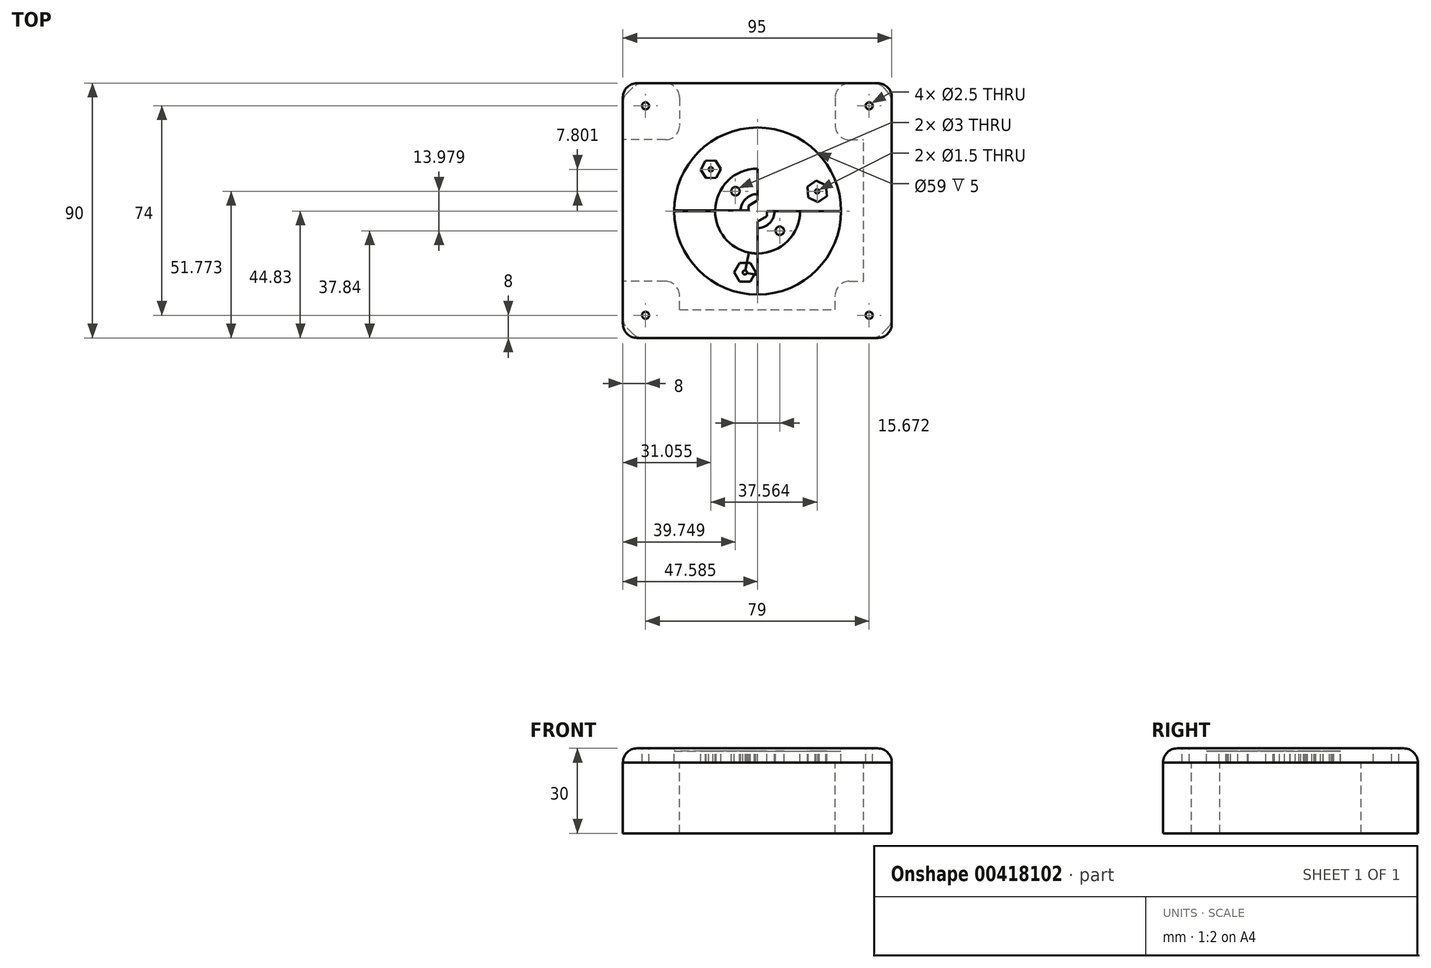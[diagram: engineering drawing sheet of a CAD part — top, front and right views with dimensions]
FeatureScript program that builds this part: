
annotation { "Feature Type Name" : "Feature", "Feature Type Description" : "" }
export const myFeature = defineFeature(function(context is Context, id is Id, definition is map)
    precondition{}
    {
        {
            var Q0;
            Q0=qCreatedBy(makeId("Top.planeOp"),FACE);
            var sketch = newSketch(context, id + "F0", { "sketchPlane" : qUnion([Q0])});
            skLineSegment(sketch, "E0", {"start": v(0, 0) * mm, "end": v(-47.5, 0) * mm});
            skLineSegment(sketch, "E1", {"start": v(-47.5, 0) * mm, "end": v(-47.5, 45) * mm});
            skLineSegment(sketch, "E2", {"start": v(-47.5, 45) * mm, "end": v(0, 45) * mm});
            skLineSegment(sketch, "E3.MirrorCS", {"start": v(47.5, 45) * mm, "end": v(0, 45) * mm});
            skLineSegment(sketch, "E4.MirrorCS", {"start": v(47.5, 0) * mm, "end": v(47.5, 45) * mm});
            skLineSegment(sketch, "E5.MirrorCS", {"start": v(-47.5, 0) * mm, "end": v(-47.5, -45) * mm});
            skLineSegment(sketch, "E6.MirrorCS", {"start": v(-47.5, -45) * mm, "end": v(0, -45) * mm});
            skLineSegment(sketch, "E7.MirrorCS", {"start": v(47.5, -45) * mm, "end": v(0, -45) * mm});
            skLineSegment(sketch, "E8.MirrorCS", {"start": v(47.5, 0) * mm, "end": v(47.5, -45) * mm});
            skLineSegment(sketch, "E9", {"start": v(-47.5, 45) * mm, "end": v(-39.5, 45) * mm});
            skLineSegment(sketch, "E10", {"start": v(-39.5, 45) * mm, "end": v(-39.5, 37) * mm});
            skCircle(sketch, "E11", {"center": v(-39.5, 37) * mm, "radius": 1.25 * mm});
            skCircle(sketch, "E12.MirrorC", {"center": v(-39.5, -37) * mm, "radius": 1.25 * mm});
            skLineSegment(sketch, "E13", {"start": v(0, 45) * mm, "end": v(0, 44.66) * mm});
            skCircle(sketch, "E14.MirrorC", {"center": v(39.5, 37) * mm, "radius": 1.25 * mm});
            skCircle(sketch, "E15.MirrorC", {"center": v(39.5, -37) * mm, "radius": 1.25 * mm});
            skCircle(sketch, "E16", {"center": v(0.08, -0.17) * mm, "radius": 29.5 * mm});
            skLineSegment(sketch, "E17", {"start": v(0.08, -0.17) * mm, "end": v(0.08, 29.33) * mm});
            skLineSegment(sketch, "E18", {"start": v(0.08, 29.33) * mm, "end": v(0.08, -29.67) * mm});
            skLineSegment(sketch, "E19", {"start": v(-29.42, -0.17) * mm, "end": v(29.58, -0.17) * mm});
            skLineSegment(sketch, "E20", {"start": v(0.08, -0.17) * mm, "end": v(-4.42, -21.86) * mm});
            skLineSegment(sketch, "E21", {"start": v(-4.42, -21.86) * mm, "end": v(0.08, -22.8) * mm});
            skCircle(sketch, "E22", {"center": v(-4.42, -21.86) * mm, "radius": 0.75 * mm});
            skCircle(sketch, "E23", {"center": v(21.12, 6.77) * mm, "radius": 0.75 * mm});
            skCircle(sketch, "E24", {"center": v(-16.44, 14.57) * mm, "radius": 0.75 * mm});
            skCircle(sketch, "E25.cCircle", {"center": v(0.08, -0.17) * mm, "radius": 3.25 * mm, "construction": true});
            skLineSegment(sketch, "E25.0", {"start": v(3.33, 1.7) * mm, "end": v(3.33, -2.05) * mm});
            skLineSegment(sketch, "E25.1", {"start": v(3.33, -2.05) * mm, "end": v(0.08, -3.92) * mm});
            skLineSegment(sketch, "E25.2", {"start": v(0.08, -3.92) * mm, "end": v(-3.17, -2.05) * mm});
            skLineSegment(sketch, "E25.3", {"start": v(-3.17, -2.05) * mm, "end": v(-3.17, 1.7) * mm});
            skLineSegment(sketch, "E25.4", {"start": v(-3.17, 1.7) * mm, "end": v(0.08, 3.58) * mm});
            skLineSegment(sketch, "E25.5", {"start": v(0.08, 3.58) * mm, "end": v(3.33, 1.7) * mm});
            skPoint(sketch, "E25.0.midPoint", {"position": v(3.33, -0.17) * mm});
            skCircle(sketch, "E26", {"center": v(0.08, -0.17) * mm, "radius": 6 * mm});
            skCircle(sketch, "E27", {"center": v(0.08, -0.17) * mm, "radius": 15 * mm});
            skLineSegment(sketch, "E28", {"start": v(8.87, -28.33) * mm, "end": v(8.87, -25.44) * mm});
            skCircle(sketch, "E29.cCircle", {"center": v(-16.44, 14.57) * mm, "radius": 3.06 * mm, "construction": true});
            skLineSegment(sketch, "E29.0", {"start": v(-14.8, 17.7) * mm, "end": v(-12.91, 14.7) * mm});
            skLineSegment(sketch, "E29.1", {"start": v(-12.91, 14.7) * mm, "end": v(-14.56, 11.58) * mm});
            skLineSegment(sketch, "E29.2", {"start": v(-14.56, 11.58) * mm, "end": v(-18.1, 11.45) * mm});
            skLineSegment(sketch, "E29.3", {"start": v(-18.1, 11.45) * mm, "end": v(-19.98, 14.44) * mm});
            skLineSegment(sketch, "E29.4", {"start": v(-19.98, 14.44) * mm, "end": v(-18.33, 17.57) * mm});
            skLineSegment(sketch, "E29.5", {"start": v(-18.33, 17.57) * mm, "end": v(-14.8, 17.7) * mm});
            skPoint(sketch, "E29.0.midPoint", {"position": v(-13.85, 16.2) * mm});
            skCircle(sketch, "E30.cCircle", {"center": v(-4.42, -21.86) * mm, "radius": 3.3 * mm, "construction": true});
            skLineSegment(sketch, "E30.0", {"start": v(-6.32, -18.56) * mm, "end": v(-2.51, -18.56) * mm});
            skLineSegment(sketch, "E30.1", {"start": v(-2.51, -18.56) * mm, "end": v(-0.6, -21.86) * mm});
            skLineSegment(sketch, "E30.2", {"start": v(-0.6, -21.86) * mm, "end": v(-2.51, -25.16) * mm});
            skLineSegment(sketch, "E30.3", {"start": v(-2.51, -25.16) * mm, "end": v(-6.32, -25.16) * mm});
            skLineSegment(sketch, "E30.4", {"start": v(-6.32, -25.16) * mm, "end": v(-8.23, -21.86) * mm});
            skLineSegment(sketch, "E30.5", {"start": v(-8.23, -21.86) * mm, "end": v(-6.32, -18.56) * mm});
            skPoint(sketch, "E30.0.midPoint", {"position": v(-4.42, -18.56) * mm});
            skCircle(sketch, "E31.cCircle", {"center": v(21.12, 6.77) * mm, "radius": 3.3 * mm, "construction": true});
            skLineSegment(sketch, "E31.0", {"start": v(20.8, 10.57) * mm, "end": v(24.24, 8.95) * mm});
            skLineSegment(sketch, "E31.1", {"start": v(24.24, 8.95) * mm, "end": v(24.57, 5.16) * mm});
            skLineSegment(sketch, "E31.2", {"start": v(24.57, 5.16) * mm, "end": v(21.45, 2.98) * mm});
            skLineSegment(sketch, "E31.3", {"start": v(21.45, 2.98) * mm, "end": v(18, 4.6) * mm});
            skLineSegment(sketch, "E31.4", {"start": v(18, 4.6) * mm, "end": v(17.67, 8.39) * mm});
            skLineSegment(sketch, "E31.5", {"start": v(17.67, 8.39) * mm, "end": v(20.8, 10.57) * mm});
            skPoint(sketch, "E31.0.midPoint", {"position": v(22.52, 9.76) * mm});
            skCircle(sketch, "E32", {"center": v(-7.75, 6.82) * mm, "radius": 1.5 * mm});
            skCircle(sketch, "E33", {"center": v(7.92, -7.16) * mm, "radius": 1.5 * mm});
            skLineSegment(sketch, "E34", {"start": v(-0.42, -25.92) * mm, "end": v(-0.42, -25.42) * mm});
            skLineSegment(sketch, "E35", {"start": v(-0.42, -25.42) * mm, "end": v(0.08, -25.42) * mm});
            skLineSegment(sketch, "E36.MirrorCS", {"start": v(0.6, -25.42) * mm, "end": v(0.08, -25.42) * mm});
            skLineSegment(sketch, "E37.MirrorCS", {"start": v(0.6, -25.92) * mm, "end": v(0.6, -25.42) * mm});
            skSolve(sketch);
        }
        {
            var Q0;
            Q0=makeQuery(id+"F0.imprint","IMPRINT",FACE,{"disambiguationData":[TD([[makeQuery(id+"F0.imprint","IMPRINT",EDGE,{"derivedFrom":sQuery(id+"F0.wireOp",EDGE,"E1")}),-1.0]])]});
            var Q1;
            Q1=makeQuery(id+"F0.imprint","IMPRINT",FACE,{"disambiguationData":[TD([[makeQuery(id+"F0.imprint","IMPRINT",EDGE,{"derivedFrom":sQuery(id+"F0.wireOp",EDGE,"RH8wCnGo-KW8f-nE2g-CZ5y-s7e0RWjT9P2i")}),1.0]])]});
            var Q2;
            Q2=makeQuery(id+"F0.imprint","IMPRINT",FACE,{"disambiguationData":[TD([[makeQuery(id+"F0.imprint","IMPRINT",EDGE,{"derivedFrom":sQuery(id+"F0.wireOp",EDGE,"E29.0")}),1.0]])]});
            var Q3;
            Q3=makeQuery(id+"F0.imprint","IMPRINT",FACE,{"disambiguationData":[TD([[makeQuery(id+"F0.imprint","IMPRINT",EDGE,{"derivedFrom":sQuery(id+"F0.wireOp",EDGE,"E32")}),-1.0]])]});
            var Q4;
            {var subQ0=sQuery(id+"F0.wireOp",EDGE,"E25.4");Q4=makeQuery(id+"F0.imprint","IMPRINT",FACE,{"disambiguationData":[TD([[makeQuery(id+"F0.imprint","IMPRINT",EDGE,{"derivedFrom":subQ0}),1.0]])]});}
            var Q5;
            {var subQ0=sQuery(id+"F0.wireOp",EDGE,"E25.1");Q5=makeQuery(id+"F0.imprint","IMPRINT",FACE,{"disambiguationData":[TD([[makeQuery(id+"F0.imprint","IMPRINT",EDGE,{"derivedFrom":subQ0}),1.0]])]});}
            var Q6;
            Q6=makeQuery(id+"F0.imprint","IMPRINT",FACE,{"disambiguationData":[TD([[makeQuery(id+"F0.imprint","IMPRINT",EDGE,{"derivedFrom":sQuery(id+"F0.wireOp",EDGE,"E33")}),-1.0]])]});
            var Q7;
            {var subQ5=sQuery(id+"F0.wireOp",EDGE,"E16");var subQ7=makeQuery(id+"F0.imprint","IMPRINT",VERTEX,{"derivedFrom":subQ5});Q7=makeQuery(id+"F0.imprint","IMPRINT",FACE,{"disambiguationData":[TD([[makeQuery(id+"F0.imprint","IMPRINT",EDGE,{"disambiguationData":[TD([[subQ7,1.0]])],"derivedFrom":subQ5}),1.0]])]});}
            var Q8;
            {var subQ13=sQuery(id+"F0.wireOp",EDGE,"E30.3");Q8=makeQuery(id+"F0.imprint","IMPRINT",FACE,{"disambiguationData":[TD([[makeQuery(id+"F0.imprint","IMPRINT",EDGE,{"derivedFrom":subQ13}),1.0]])]});}
            var Q9;
            Q9=makeQuery(id+"F0.imprint","IMPRINT",FACE,{"disambiguationData":[TD([[makeQuery(id+"F0.imprint","IMPRINT",EDGE,{"derivedFrom":sQuery(id+"F0.wireOp",EDGE,"E31.0")}),1.0]])]});
            var Q10;
            {var subQ8=sQuery(id+"F0.wireOp",EDGE,"E30.1");Q10=makeQuery(id+"F0.imprint","IMPRINT",FACE,{"disambiguationData":[TD([[makeQuery(id+"F0.imprint","IMPRINT",EDGE,{"derivedFrom":subQ8}),1.0]])]});}
            var Q11;
            {var subQ0=sQuery(id+"F0.wireOp",EDGE,"E16");var subQ1=sQuery(id+"F0.wireOp",EDGE,"E0");var subQ2=makeQuery(id+"F0.imprint","INTERSECT",VERTEX,{"derivedFrom":[subQ1,subQ0]});Q11=makeQuery(id+"F0.imprint","IMPRINT",FACE,{"disambiguationData":[TD([[makeQuery(id+"F0.imprint","IMPRINT",EDGE,{"disambiguationData":[TD([[subQ2,1.0]])],"derivedFrom":subQ1}),1.0]])]});}
            var Q12;
            Q12=makeQuery(id+"F0.imprint","IMPRINT",FACE,{"disambiguationData":[TD([[makeQuery(id+"F0.imprint","IMPRINT",EDGE,{"derivedFrom":sQuery(id+"F0.wireOp",EDGE,"E23")}),-1.0]])]});
            var Q13;
            {var subQ5=sQuery(id+"F0.wireOp",EDGE,"E30.1");Q13=makeQuery(id+"F0.imprint","IMPRINT",FACE,{"disambiguationData":[TD([[makeQuery(id+"F0.imprint","IMPRINT",EDGE,{"derivedFrom":subQ5}),-1.0]])]});}
            var Q14;
            {var subQ10=sQuery(id+"F0.wireOp",EDGE,"E30.3");Q14=makeQuery(id+"F0.imprint","IMPRINT",FACE,{"disambiguationData":[TD([[makeQuery(id+"F0.imprint","IMPRINT",EDGE,{"derivedFrom":subQ10}),-1.0]])]});}
            var Q15;
            Q15=makeQuery(id+"F0.imprint","IMPRINT",FACE,{"disambiguationData":[TD([[makeQuery(id+"F0.imprint","IMPRINT",EDGE,{"derivedFrom":sQuery(id+"F0.wireOp",EDGE,"E24")}),-1.0]])]});
            extrude(context, id + "F1", {"entities" : qUnion([Q0, Q1, Q2, Q3, Q4, Q5, Q6, Q7, Q8, Q9, Q10, Q11, Q12, Q13, Q14, Q15]), "oppositeDirection" : true, "depth" : 5 * mm});
        }
        {
            var Q0;
            Q0=makeQuery(id+"F0.imprint","IMPRINT",FACE,{"disambiguationData":[TD([[makeQuery(id+"F0.imprint","IMPRINT",EDGE,{"derivedFrom":sQuery(id+"F0.wireOp",EDGE,"E31.0")}),1.0]])]});
            var Q1;
            {var subQ5=sQuery(id+"F0.wireOp",EDGE,"E16");var subQ7=makeQuery(id+"F0.imprint","IMPRINT",VERTEX,{"derivedFrom":subQ5});Q1=makeQuery(id+"F0.imprint","IMPRINT",FACE,{"disambiguationData":[TD([[makeQuery(id+"F0.imprint","IMPRINT",EDGE,{"disambiguationData":[TD([[subQ7,1.0]])],"derivedFrom":subQ5}),1.0]])]});}
            var Q2;
            Q2=makeQuery(id+"F0.imprint","IMPRINT",FACE,{"disambiguationData":[TD([[makeQuery(id+"F0.imprint","IMPRINT",EDGE,{"derivedFrom":sQuery(id+"F0.wireOp",EDGE,"E33")}),-1.0]])]});
            var Q3;
            {var subQ13=sQuery(id+"F0.wireOp",EDGE,"E30.3");Q3=makeQuery(id+"F0.imprint","IMPRINT",FACE,{"disambiguationData":[TD([[makeQuery(id+"F0.imprint","IMPRINT",EDGE,{"derivedFrom":subQ13}),1.0]])]});}
            var Q4;
            Q4=makeQuery(id+"F0.imprint","IMPRINT",FACE,{"disambiguationData":[TD([[makeQuery(id+"F0.imprint","IMPRINT",EDGE,{"derivedFrom":sQuery(id+"F0.wireOp",EDGE,"E32")}),-1.0]])]});
            var Q5;
            Q5=makeQuery(id+"F0.imprint","IMPRINT",FACE,{"disambiguationData":[TD([[makeQuery(id+"F0.imprint","IMPRINT",EDGE,{"derivedFrom":sQuery(id+"F0.wireOp",EDGE,"E29.0")}),1.0]])]});
            var Q6;
            {var subQ0=sQuery(id+"F0.wireOp",EDGE,"E25.4");Q6=makeQuery(id+"F0.imprint","IMPRINT",FACE,{"disambiguationData":[TD([[makeQuery(id+"F0.imprint","IMPRINT",EDGE,{"derivedFrom":subQ0}),1.0]])]});}
            var Q7;
            {var subQ0=sQuery(id+"F0.wireOp",EDGE,"E25.1");Q7=makeQuery(id+"F0.imprint","IMPRINT",FACE,{"disambiguationData":[TD([[makeQuery(id+"F0.imprint","IMPRINT",EDGE,{"derivedFrom":subQ0}),1.0]])]});}
            var Q8;
            {var subQ8=sQuery(id+"F0.wireOp",EDGE,"E30.1");Q8=makeQuery(id+"F0.imprint","IMPRINT",FACE,{"disambiguationData":[TD([[makeQuery(id+"F0.imprint","IMPRINT",EDGE,{"derivedFrom":subQ8}),1.0]])]});}
            var Q9;
            {var subQ0=sQuery(id+"F0.wireOp",EDGE,"E16");var subQ1=sQuery(id+"F0.wireOp",EDGE,"E0");var subQ2=makeQuery(id+"F0.imprint","INTERSECT",VERTEX,{"derivedFrom":[subQ1,subQ0]});Q9=makeQuery(id+"F0.imprint","IMPRINT",FACE,{"disambiguationData":[TD([[makeQuery(id+"F0.imprint","IMPRINT",EDGE,{"disambiguationData":[TD([[subQ2,1.0]])],"derivedFrom":subQ1}),1.0]])]});}
            var Q10;
            Q10=makeQuery(id+"F0.imprint","IMPRINT",FACE,{"disambiguationData":[TD([[makeQuery(id+"F0.imprint","IMPRINT",EDGE,{"derivedFrom":sQuery(id+"F0.wireOp",EDGE,"E24")}),-1.0]])]});
            var Q11;
            {var subQ5=sQuery(id+"F0.wireOp",EDGE,"E30.1");Q11=makeQuery(id+"F0.imprint","IMPRINT",FACE,{"disambiguationData":[TD([[makeQuery(id+"F0.imprint","IMPRINT",EDGE,{"derivedFrom":subQ5}),-1.0]])]});}
            var Q12;
            {var subQ10=sQuery(id+"F0.wireOp",EDGE,"E30.3");Q12=makeQuery(id+"F0.imprint","IMPRINT",FACE,{"disambiguationData":[TD([[makeQuery(id+"F0.imprint","IMPRINT",EDGE,{"derivedFrom":subQ10}),-1.0]])]});}
            var Q13;
            Q13=makeQuery(id+"F0.imprint","IMPRINT",FACE,{"disambiguationData":[TD([[makeQuery(id+"F0.imprint","IMPRINT",EDGE,{"derivedFrom":sQuery(id+"F0.wireOp",EDGE,"E23")}),-1.0]])]});
            extrude(context, id + "F2", {"entities" : qUnion([Q0, Q1, Q2, Q3, Q4, Q5, Q6, Q7, Q8, Q9, Q10, Q11, Q12, Q13]), "operationType" : NewBodyOperationType.REMOVE, "oppositeDirection" : true, "depth" : 1 * mm});
        }
        {
            var Q0;
            Q0=makeQuery(id+"F1.opExtrude","CAP_EDGE",EDGE,{"disambiguationData":[OSD([sQuery(id+"F0.wireOp",EDGE,"E1"),sQuery(id+"F0.wireOp",EDGE,"E5.MirrorCS")])],"isStart":true});
            var Q1;
            Q1=makeQuery(id+"F1.opExtrude","CAP_EDGE",EDGE,{"disambiguationData":[OSD([sQuery(id+"F0.wireOp",EDGE,"E2"),sQuery(id+"F0.wireOp",EDGE,"E3.MirrorCS"),sQuery(id+"F0.wireOp",EDGE,"E9")])],"isStart":true});
            var Q2;
            Q2=makeQuery(id+"F1.opExtrude","CAP_EDGE",EDGE,{"disambiguationData":[OSD([sQuery(id+"F0.wireOp",EDGE,"E6.MirrorCS"),sQuery(id+"F0.wireOp",EDGE,"E7.MirrorCS")])],"isStart":true});
            var Q3;
            Q3=makeQuery(id+"F1.opExtrude","CAP_EDGE",EDGE,{"disambiguationData":[OSD([sQuery(id+"F0.wireOp",EDGE,"E4.MirrorCS"),sQuery(id+"F0.wireOp",EDGE,"E8.MirrorCS")])],"isStart":true});
            var Q4;
            Q4=makeQuery(id+"F1.opExtrude","SWEPT_EDGE",EDGE,{"disambiguationData":[OSD([sQuery(id+"F0.wireOp",EDGE,"E7.MirrorCS"),sQuery(id+"F0.wireOp",EDGE,"E8.MirrorCS")])]});
            var Q5;
            Q5=makeQuery(id+"F1.opExtrude","SWEPT_EDGE",EDGE,{"disambiguationData":[OSD([sQuery(id+"F0.wireOp",EDGE,"E5.MirrorCS"),sQuery(id+"F0.wireOp",EDGE,"E6.MirrorCS")])]});
            var Q6;
            Q6=makeQuery(id+"F1.opExtrude","SWEPT_EDGE",EDGE,{"disambiguationData":[OSD([sQuery(id+"F0.wireOp",EDGE,"E1"),sQuery(id+"F0.wireOp",EDGE,"E9")])]});
            var Q7;
            Q7=makeQuery(id+"F1.opExtrude","SWEPT_EDGE",EDGE,{"disambiguationData":[OSD([sQuery(id+"F0.wireOp",EDGE,"E3.MirrorCS"),sQuery(id+"F0.wireOp",EDGE,"E4.MirrorCS")])]});
            fillet(context, id + "F3", {"entities" : qUnion([Q0, Q1, Q2, Q3, Q4, Q5, Q6, Q7]), "radius" : 5 * mm, "tangentPropagation" : true, "allowEdgeOverflow" : false});
        }
        {
            var Q0;
            Q0=makeQuery(id+"F1.opExtrude","CAP_FACE",FACE,{"disambiguationData":[OSD([sQuery(id+"F0.wireOp",EDGE,"E0"),sQuery(id+"F0.wireOp",EDGE,"E1"),sQuery(id+"F0.wireOp",EDGE,"E2"),sQuery(id+"F0.wireOp",EDGE,"E3.MirrorCS"),sQuery(id+"F0.wireOp",EDGE,"E4.MirrorCS"),sQuery(id+"F0.wireOp",EDGE,"E5.MirrorCS"),sQuery(id+"F0.wireOp",EDGE,"E6.MirrorCS"),sQuery(id+"F0.wireOp",EDGE,"E7.MirrorCS"),sQuery(id+"F0.wireOp",EDGE,"E8.MirrorCS"),sQuery(id+"F0.wireOp",EDGE,"E9"),sQuery(id+"F0.wireOp",EDGE,"E11"),sQuery(id+"F0.wireOp",EDGE,"E12.MirrorC"),sQuery(id+"F0.wireOp",EDGE,"E14.MirrorC"),sQuery(id+"F0.wireOp",EDGE,"E15.MirrorC"),sQuery(id+"F0.wireOp",EDGE,"E18"),sQuery(id+"F0.wireOp",EDGE,"E19"),sQuery(id+"F0.wireOp",EDGE,"E22"),sQuery(id+"F0.wireOp",EDGE,"E23"),sQuery(id+"F0.wireOp",EDGE,"E24"),sQuery(id+"F0.wireOp",EDGE,"E25.0"),sQuery(id+"F0.wireOp",EDGE,"E25.1"),sQuery(id+"F0.wireOp",EDGE,"E25.3"),sQuery(id+"F0.wireOp",EDGE,"E25.4"),sQuery(id+"F0.wireOp",EDGE,"E27"),sQuery(id+"F0.wireOp",EDGE,"E32"),sQuery(id+"F0.wireOp",EDGE,"E33")])],"isStart":false});
            var sketch = newSketch(context, id + "F4", { "sketchPlane" : qUnion([Q0])});
            skLineSegment(sketch, "E38", {"start": v(-39.5, 37) * mm, "end": v(-39.5, 45) * mm});
            skLineSegment(sketch, "E39", {"start": v(47.5, 40) * mm, "end": v(42.5, 45) * mm});
            skLineSegment(sketch, "E40", {"start": v(47.5, -40) * mm, "end": v(43.5, -44.9) * mm});
            skLineSegment(sketch, "E41", {"start": v(43.5, -44.9) * mm, "end": v(-42.5, -45) * mm});
            skLineSegment(sketch, "E42", {"start": v(-42.5, -45) * mm, "end": v(-47.5, -40) * mm});
            skLineSegment(sketch, "E43", {"start": v(-47.5, -40) * mm, "end": v(-47.5, 40) * mm});
            skLineSegment(sketch, "E44", {"start": v(-47.5, 40) * mm, "end": v(-42.5, 45) * mm});
            skLineSegment(sketch, "E45", {"start": v(-42.5, 45) * mm, "end": v(-39.5, 45) * mm});
            skLineSegment(sketch, "E46", {"start": v(42.5, 45) * mm, "end": v(-39.5, 45) * mm});
            skPoint(sketch, "E47.start.orphan", {"position": v(47.5, 45) * mm});
            skLineSegment(sketch, "E48", {"start": v(47.5, 40) * mm, "end": v(47.5, -40) * mm});
            skLineSegment(sketch, "E49", {"start": v(-27.5, 45) * mm, "end": v(-27.5, 25) * mm});
            skLineSegment(sketch, "E50", {"start": v(-27.5, 25) * mm, "end": v(-47.5, 25) * mm});
            skLineSegment(sketch, "E51", {"start": v(-47.5, 0) * mm, "end": v(-37.34, 0) * mm});
            skLineSegment(sketch, "E52", {"start": v(0, 45) * mm, "end": v(0, 40.69) * mm});
            skLineSegment(sketch, "E53.MirrorCS", {"start": v(27.5, 45) * mm, "end": v(27.5, 25) * mm});
            skLineSegment(sketch, "E54.MirrorCS", {"start": v(27.5, 25) * mm, "end": v(47.5, 25) * mm});
            skLineSegment(sketch, "E55.MirrorCS", {"start": v(-27.5, -25) * mm, "end": v(-47.5, -25) * mm});
            skLineSegment(sketch, "E56.MirrorCS", {"start": v(-27.5, -45) * mm, "end": v(-27.5, -25) * mm});
            skLineSegment(sketch, "E57.MirrorCS", {"start": v(27.5, -45) * mm, "end": v(27.5, -25) * mm});
            skLineSegment(sketch, "E58.MirrorCS", {"start": v(27.5, -25) * mm, "end": v(47.5, -25) * mm});
            skLineSegment(sketch, "E59", {"start": v(-27.5, 35) * mm, "end": v(27.5, 35) * mm});
            skLineSegment(sketch, "E60", {"start": v(27.5, -35) * mm, "end": v(-27.5, -35) * mm});
            skLineSegment(sketch, "E61", {"start": v(-37.5, -25) * mm, "end": v(-37.5, 25) * mm});
            skLineSegment(sketch, "E62", {"start": v(37.5, 25) * mm, "end": v(37.5, -25) * mm});
            skSolve(sketch);
        }
        {
            var Q0;
            {var subQ5=sQuery(id+"F4.wireOp",EDGE,"E40");Q0=makeQuery(id+"F4.imprint","IMPRINT",FACE,{"disambiguationData":[TD([[makeQuery(id+"F4.imprint","IMPRINT",EDGE,{"derivedFrom":subQ5}),-1.0]])]});}
            var Q1;
            {var subQ0=sQuery(id+"F4.wireOp",EDGE,"E42");Q1=makeQuery(id+"F4.imprint","IMPRINT",FACE,{"disambiguationData":[TD([[makeQuery(id+"F4.imprint","IMPRINT",EDGE,{"derivedFrom":subQ0}),-1.0]])]});}
            var Q2;
            {var subQ0=sQuery(id+"F4.wireOp",EDGE,"E53.MirrorCS");Q2=makeQuery(id+"F4.imprint","IMPRINT",FACE,{"disambiguationData":[TD([[makeQuery(id+"F4.imprint","IMPRINT",EDGE,{"derivedFrom":subQ0}),1.0]])]});}
            var Q3;
            {var subQ1=sQuery(id+"F4.wireOp",EDGE,"E44");Q3=makeQuery(id+"F4.imprint","IMPRINT",FACE,{"disambiguationData":[TD([[makeQuery(id+"F4.imprint","IMPRINT",EDGE,{"derivedFrom":subQ1}),-1.0]])]});}
            var Q4;
            {var subQ3=sQuery(id+"F4.wireOp",EDGE,"E59");Q4=makeQuery(id+"F4.imprint","IMPRINT",FACE,{"disambiguationData":[TD([[makeQuery(id+"F4.imprint","IMPRINT",EDGE,{"derivedFrom":subQ3}),1.0]])]});}
            var Q5;
            {var subQ0=sQuery(id+"F4.wireOp",EDGE,"E50");var subQ1=sQuery(id+"F4.wireOp",EDGE,"E43");var subQ2=makeQuery(id+"F4.imprint","INTERSECT",VERTEX,{"derivedFrom":[subQ1,subQ0]});Q5=makeQuery(id+"F4.imprint","IMPRINT",FACE,{"disambiguationData":[TD([[makeQuery(id+"F4.imprint","IMPRINT",EDGE,{"disambiguationData":[TD([[subQ2,-1.0]])],"derivedFrom":subQ1}),1.0]])]});}
            var Q6;
            {var subQ0=sQuery(id+"F4.wireOp",EDGE,"E51");var subQ1=sQuery(id+"F4.wireOp",EDGE,"E43");var subQ2=makeQuery(id+"F4.imprint","INTERSECT",VERTEX,{"derivedFrom":[subQ1,subQ0]});Q6=makeQuery(id+"F4.imprint","IMPRINT",FACE,{"disambiguationData":[TD([[makeQuery(id+"F4.imprint","IMPRINT",EDGE,{"disambiguationData":[TD([[subQ2,-1.0]])],"derivedFrom":subQ1}),1.0]])]});}
            var Q7;
            {var subQ5=sQuery(id+"F4.wireOp",EDGE,"E62");Q7=makeQuery(id+"F4.imprint","IMPRINT",FACE,{"disambiguationData":[TD([[makeQuery(id+"F4.imprint","IMPRINT",EDGE,{"derivedFrom":subQ5}),1.0]])]});}
            extrude(context, id + "F5", {"entities" : qUnion([Q0, Q1, Q2, Q3, Q4, Q5, Q6, Q7]), "depth" : 25 * mm});
        }
        {
            var Q0;
            Q0=makeQuery(id+"F5.opExtrude","SWEPT_EDGE",EDGE,{"disambiguationData":[OSD([sQuery(id+"F0.wireOp",EDGE,"E0"),sQuery(id+"F0.wireOp",EDGE,"E1"),sQuery(id+"F0.wireOp",EDGE,"E2"),sQuery(id+"F0.wireOp",EDGE,"E3.MirrorCS"),sQuery(id+"F0.wireOp",EDGE,"E4.MirrorCS"),sQuery(id+"F0.wireOp",EDGE,"E5.MirrorCS"),sQuery(id+"F0.wireOp",EDGE,"E6.MirrorCS"),sQuery(id+"F0.wireOp",EDGE,"E7.MirrorCS"),sQuery(id+"F0.wireOp",EDGE,"E8.MirrorCS"),sQuery(id+"F0.wireOp",EDGE,"E9"),sQuery(id+"F0.wireOp",EDGE,"E11"),sQuery(id+"F0.wireOp",EDGE,"E12.MirrorC"),sQuery(id+"F0.wireOp",EDGE,"E14.MirrorC"),sQuery(id+"F0.wireOp",EDGE,"E15.MirrorC"),sQuery(id+"F0.wireOp",EDGE,"E18"),sQuery(id+"F0.wireOp",EDGE,"E19"),sQuery(id+"F0.wireOp",EDGE,"E22"),sQuery(id+"F0.wireOp",EDGE,"E23"),sQuery(id+"F0.wireOp",EDGE,"E24"),sQuery(id+"F0.wireOp",EDGE,"E25.0"),sQuery(id+"F0.wireOp",EDGE,"E25.1"),sQuery(id+"F0.wireOp",EDGE,"E25.3"),sQuery(id+"F0.wireOp",EDGE,"E25.4"),sQuery(id+"F0.wireOp",EDGE,"E27"),sQuery(id+"F0.wireOp",EDGE,"E32"),sQuery(id+"F0.wireOp",EDGE,"E33"),sQuery(id+"F4.wireOp",EDGE,"E44"),sQuery(id+"F4.wireOp",EDGE,"E45")])]});
            var Q1;
            Q1=makeQuery(id+"F5.opExtrude","SWEPT_EDGE",EDGE,{"disambiguationData":[OSD([sQuery(id+"F0.wireOp",EDGE,"E0"),sQuery(id+"F0.wireOp",EDGE,"E1"),sQuery(id+"F0.wireOp",EDGE,"E2"),sQuery(id+"F0.wireOp",EDGE,"E3.MirrorCS"),sQuery(id+"F0.wireOp",EDGE,"E4.MirrorCS"),sQuery(id+"F0.wireOp",EDGE,"E5.MirrorCS"),sQuery(id+"F0.wireOp",EDGE,"E6.MirrorCS"),sQuery(id+"F0.wireOp",EDGE,"E7.MirrorCS"),sQuery(id+"F0.wireOp",EDGE,"E8.MirrorCS"),sQuery(id+"F0.wireOp",EDGE,"E9"),sQuery(id+"F0.wireOp",EDGE,"E11"),sQuery(id+"F0.wireOp",EDGE,"E12.MirrorC"),sQuery(id+"F0.wireOp",EDGE,"E14.MirrorC"),sQuery(id+"F0.wireOp",EDGE,"E15.MirrorC"),sQuery(id+"F0.wireOp",EDGE,"E18"),sQuery(id+"F0.wireOp",EDGE,"E19"),sQuery(id+"F0.wireOp",EDGE,"E22"),sQuery(id+"F0.wireOp",EDGE,"E23"),sQuery(id+"F0.wireOp",EDGE,"E24"),sQuery(id+"F0.wireOp",EDGE,"E25.0"),sQuery(id+"F0.wireOp",EDGE,"E25.1"),sQuery(id+"F0.wireOp",EDGE,"E25.3"),sQuery(id+"F0.wireOp",EDGE,"E25.4"),sQuery(id+"F0.wireOp",EDGE,"E27"),sQuery(id+"F0.wireOp",EDGE,"E32"),sQuery(id+"F0.wireOp",EDGE,"E33"),sQuery(id+"F4.wireOp",EDGE,"E46"),sQuery(id+"F4.wireOp",EDGE,"E39")])]});
            var Q2;
            Q2=makeQuery(id+"F5.opExtrude","SWEPT_EDGE",EDGE,{"disambiguationData":[OSD([sQuery(id+"F0.wireOp",EDGE,"E0"),sQuery(id+"F0.wireOp",EDGE,"E1"),sQuery(id+"F0.wireOp",EDGE,"E2"),sQuery(id+"F0.wireOp",EDGE,"E3.MirrorCS"),sQuery(id+"F0.wireOp",EDGE,"E4.MirrorCS"),sQuery(id+"F0.wireOp",EDGE,"E5.MirrorCS"),sQuery(id+"F0.wireOp",EDGE,"E6.MirrorCS"),sQuery(id+"F0.wireOp",EDGE,"E7.MirrorCS"),sQuery(id+"F0.wireOp",EDGE,"E8.MirrorCS"),sQuery(id+"F0.wireOp",EDGE,"E9"),sQuery(id+"F0.wireOp",EDGE,"E11"),sQuery(id+"F0.wireOp",EDGE,"E12.MirrorC"),sQuery(id+"F0.wireOp",EDGE,"E14.MirrorC"),sQuery(id+"F0.wireOp",EDGE,"E15.MirrorC"),sQuery(id+"F0.wireOp",EDGE,"E18"),sQuery(id+"F0.wireOp",EDGE,"E19"),sQuery(id+"F0.wireOp",EDGE,"E22"),sQuery(id+"F0.wireOp",EDGE,"E23"),sQuery(id+"F0.wireOp",EDGE,"E24"),sQuery(id+"F0.wireOp",EDGE,"E25.0"),sQuery(id+"F0.wireOp",EDGE,"E25.1"),sQuery(id+"F0.wireOp",EDGE,"E25.3"),sQuery(id+"F0.wireOp",EDGE,"E25.4"),sQuery(id+"F0.wireOp",EDGE,"E27"),sQuery(id+"F0.wireOp",EDGE,"E32"),sQuery(id+"F0.wireOp",EDGE,"E33"),sQuery(id+"F4.wireOp",EDGE,"E48"),sQuery(id+"F4.wireOp",EDGE,"E39")])]});
            var Q3;
            Q3=makeQuery(id+"F5.opExtrude","SWEPT_EDGE",EDGE,{"disambiguationData":[OSD([sQuery(id+"F0.wireOp",EDGE,"E0"),sQuery(id+"F0.wireOp",EDGE,"E1"),sQuery(id+"F0.wireOp",EDGE,"E2"),sQuery(id+"F0.wireOp",EDGE,"E3.MirrorCS"),sQuery(id+"F0.wireOp",EDGE,"E4.MirrorCS"),sQuery(id+"F0.wireOp",EDGE,"E5.MirrorCS"),sQuery(id+"F0.wireOp",EDGE,"E6.MirrorCS"),sQuery(id+"F0.wireOp",EDGE,"E7.MirrorCS"),sQuery(id+"F0.wireOp",EDGE,"E8.MirrorCS"),sQuery(id+"F0.wireOp",EDGE,"E9"),sQuery(id+"F0.wireOp",EDGE,"E11"),sQuery(id+"F0.wireOp",EDGE,"E12.MirrorC"),sQuery(id+"F0.wireOp",EDGE,"E14.MirrorC"),sQuery(id+"F0.wireOp",EDGE,"E15.MirrorC"),sQuery(id+"F0.wireOp",EDGE,"E18"),sQuery(id+"F0.wireOp",EDGE,"E19"),sQuery(id+"F0.wireOp",EDGE,"E22"),sQuery(id+"F0.wireOp",EDGE,"E23"),sQuery(id+"F0.wireOp",EDGE,"E24"),sQuery(id+"F0.wireOp",EDGE,"E25.0"),sQuery(id+"F0.wireOp",EDGE,"E25.1"),sQuery(id+"F0.wireOp",EDGE,"E25.3"),sQuery(id+"F0.wireOp",EDGE,"E25.4"),sQuery(id+"F0.wireOp",EDGE,"E27"),sQuery(id+"F0.wireOp",EDGE,"E32"),sQuery(id+"F0.wireOp",EDGE,"E33"),sQuery(id+"F4.wireOp",EDGE,"E40"),sQuery(id+"F4.wireOp",EDGE,"E48")])]});
            var Q4;
            Q4=makeQuery(id+"F5.opExtrude","SWEPT_EDGE",EDGE,{"disambiguationData":[OSD([sQuery(id+"F0.wireOp",EDGE,"E0"),sQuery(id+"F0.wireOp",EDGE,"E1"),sQuery(id+"F0.wireOp",EDGE,"E2"),sQuery(id+"F0.wireOp",EDGE,"E3.MirrorCS"),sQuery(id+"F0.wireOp",EDGE,"E4.MirrorCS"),sQuery(id+"F0.wireOp",EDGE,"E5.MirrorCS"),sQuery(id+"F0.wireOp",EDGE,"E6.MirrorCS"),sQuery(id+"F0.wireOp",EDGE,"E7.MirrorCS"),sQuery(id+"F0.wireOp",EDGE,"E8.MirrorCS"),sQuery(id+"F0.wireOp",EDGE,"E9"),sQuery(id+"F0.wireOp",EDGE,"E11"),sQuery(id+"F0.wireOp",EDGE,"E12.MirrorC"),sQuery(id+"F0.wireOp",EDGE,"E14.MirrorC"),sQuery(id+"F0.wireOp",EDGE,"E15.MirrorC"),sQuery(id+"F0.wireOp",EDGE,"E18"),sQuery(id+"F0.wireOp",EDGE,"E19"),sQuery(id+"F0.wireOp",EDGE,"E22"),sQuery(id+"F0.wireOp",EDGE,"E23"),sQuery(id+"F0.wireOp",EDGE,"E24"),sQuery(id+"F0.wireOp",EDGE,"E25.0"),sQuery(id+"F0.wireOp",EDGE,"E25.1"),sQuery(id+"F0.wireOp",EDGE,"E25.3"),sQuery(id+"F0.wireOp",EDGE,"E25.4"),sQuery(id+"F0.wireOp",EDGE,"E27"),sQuery(id+"F0.wireOp",EDGE,"E32"),sQuery(id+"F0.wireOp",EDGE,"E33"),sQuery(id+"F4.wireOp",EDGE,"E40"),sQuery(id+"F4.wireOp",EDGE,"E41")])]});
            var Q5;
            Q5=makeQuery(id+"F5.opExtrude","SWEPT_EDGE",EDGE,{"disambiguationData":[OSD([sQuery(id+"F0.wireOp",EDGE,"E0"),sQuery(id+"F0.wireOp",EDGE,"E1"),sQuery(id+"F0.wireOp",EDGE,"E2"),sQuery(id+"F0.wireOp",EDGE,"E3.MirrorCS"),sQuery(id+"F0.wireOp",EDGE,"E4.MirrorCS"),sQuery(id+"F0.wireOp",EDGE,"E5.MirrorCS"),sQuery(id+"F0.wireOp",EDGE,"E6.MirrorCS"),sQuery(id+"F0.wireOp",EDGE,"E7.MirrorCS"),sQuery(id+"F0.wireOp",EDGE,"E8.MirrorCS"),sQuery(id+"F0.wireOp",EDGE,"E9"),sQuery(id+"F0.wireOp",EDGE,"E11"),sQuery(id+"F0.wireOp",EDGE,"E12.MirrorC"),sQuery(id+"F0.wireOp",EDGE,"E14.MirrorC"),sQuery(id+"F0.wireOp",EDGE,"E15.MirrorC"),sQuery(id+"F0.wireOp",EDGE,"E18"),sQuery(id+"F0.wireOp",EDGE,"E19"),sQuery(id+"F0.wireOp",EDGE,"E22"),sQuery(id+"F0.wireOp",EDGE,"E23"),sQuery(id+"F0.wireOp",EDGE,"E24"),sQuery(id+"F0.wireOp",EDGE,"E25.0"),sQuery(id+"F0.wireOp",EDGE,"E25.1"),sQuery(id+"F0.wireOp",EDGE,"E25.3"),sQuery(id+"F0.wireOp",EDGE,"E25.4"),sQuery(id+"F0.wireOp",EDGE,"E27"),sQuery(id+"F0.wireOp",EDGE,"E32"),sQuery(id+"F0.wireOp",EDGE,"E33"),sQuery(id+"F4.wireOp",EDGE,"E41"),sQuery(id+"F4.wireOp",EDGE,"E42")])]});
            var Q6;
            Q6=makeQuery(id+"F5.opExtrude","SWEPT_EDGE",EDGE,{"disambiguationData":[OSD([sQuery(id+"F0.wireOp",EDGE,"E0"),sQuery(id+"F0.wireOp",EDGE,"E1"),sQuery(id+"F0.wireOp",EDGE,"E2"),sQuery(id+"F0.wireOp",EDGE,"E3.MirrorCS"),sQuery(id+"F0.wireOp",EDGE,"E4.MirrorCS"),sQuery(id+"F0.wireOp",EDGE,"E5.MirrorCS"),sQuery(id+"F0.wireOp",EDGE,"E6.MirrorCS"),sQuery(id+"F0.wireOp",EDGE,"E7.MirrorCS"),sQuery(id+"F0.wireOp",EDGE,"E8.MirrorCS"),sQuery(id+"F0.wireOp",EDGE,"E9"),sQuery(id+"F0.wireOp",EDGE,"E11"),sQuery(id+"F0.wireOp",EDGE,"E12.MirrorC"),sQuery(id+"F0.wireOp",EDGE,"E14.MirrorC"),sQuery(id+"F0.wireOp",EDGE,"E15.MirrorC"),sQuery(id+"F0.wireOp",EDGE,"E18"),sQuery(id+"F0.wireOp",EDGE,"E19"),sQuery(id+"F0.wireOp",EDGE,"E22"),sQuery(id+"F0.wireOp",EDGE,"E23"),sQuery(id+"F0.wireOp",EDGE,"E24"),sQuery(id+"F0.wireOp",EDGE,"E25.0"),sQuery(id+"F0.wireOp",EDGE,"E25.1"),sQuery(id+"F0.wireOp",EDGE,"E25.3"),sQuery(id+"F0.wireOp",EDGE,"E25.4"),sQuery(id+"F0.wireOp",EDGE,"E27"),sQuery(id+"F0.wireOp",EDGE,"E32"),sQuery(id+"F0.wireOp",EDGE,"E33"),sQuery(id+"F4.wireOp",EDGE,"E42"),sQuery(id+"F4.wireOp",EDGE,"E43")])]});
            var Q7;
            Q7=makeQuery(id+"F5.opExtrude","SWEPT_EDGE",EDGE,{"disambiguationData":[OSD([sQuery(id+"F4.wireOp",EDGE,"E41"),sQuery(id+"F4.wireOp",EDGE,"E56.MirrorCS")])]});
            var Q8;
            Q8=makeQuery(id+"F5.opExtrude","SWEPT_EDGE",EDGE,{"disambiguationData":[OSD([sQuery(id+"F4.wireOp",EDGE,"E53.MirrorCS"),sQuery(id+"F4.wireOp",EDGE,"E54.MirrorCS")])]});
            var Q9;
            Q9=makeQuery(id+"F5.opExtrude","SWEPT_EDGE",EDGE,{"disambiguationData":[OSD([sQuery(id+"F4.wireOp",EDGE,"E49"),sQuery(id+"F4.wireOp",EDGE,"E50")])]});
            var Q10;
            Q10=makeQuery(id+"F5.opExtrude","SWEPT_EDGE",EDGE,{"disambiguationData":[OSD([sQuery(id+"F4.wireOp",EDGE,"E55.MirrorCS"),sQuery(id+"F4.wireOp",EDGE,"E56.MirrorCS")])]});
            var Q11;
            Q11=makeQuery(id+"F5.opExtrude","SWEPT_EDGE",EDGE,{"disambiguationData":[OSD([sQuery(id+"F4.wireOp",EDGE,"E57.MirrorCS"),sQuery(id+"F4.wireOp",EDGE,"E58.MirrorCS")])]});
            var Q12;
            Q12=makeQuery(id+"F5.opExtrude","SWEPT_EDGE",EDGE,{"disambiguationData":[OSD([sQuery(id+"F0.wireOp",EDGE,"E0"),sQuery(id+"F0.wireOp",EDGE,"E1"),sQuery(id+"F0.wireOp",EDGE,"E2"),sQuery(id+"F0.wireOp",EDGE,"E3.MirrorCS"),sQuery(id+"F0.wireOp",EDGE,"E4.MirrorCS"),sQuery(id+"F0.wireOp",EDGE,"E5.MirrorCS"),sQuery(id+"F0.wireOp",EDGE,"E6.MirrorCS"),sQuery(id+"F0.wireOp",EDGE,"E7.MirrorCS"),sQuery(id+"F0.wireOp",EDGE,"E8.MirrorCS"),sQuery(id+"F0.wireOp",EDGE,"E9"),sQuery(id+"F0.wireOp",EDGE,"E11"),sQuery(id+"F0.wireOp",EDGE,"E12.MirrorC"),sQuery(id+"F0.wireOp",EDGE,"E14.MirrorC"),sQuery(id+"F0.wireOp",EDGE,"E15.MirrorC"),sQuery(id+"F0.wireOp",EDGE,"E18"),sQuery(id+"F0.wireOp",EDGE,"E19"),sQuery(id+"F0.wireOp",EDGE,"E22"),sQuery(id+"F0.wireOp",EDGE,"E23"),sQuery(id+"F0.wireOp",EDGE,"E24"),sQuery(id+"F0.wireOp",EDGE,"E25.0"),sQuery(id+"F0.wireOp",EDGE,"E25.1"),sQuery(id+"F0.wireOp",EDGE,"E25.3"),sQuery(id+"F0.wireOp",EDGE,"E25.4"),sQuery(id+"F0.wireOp",EDGE,"E27"),sQuery(id+"F0.wireOp",EDGE,"E32"),sQuery(id+"F0.wireOp",EDGE,"E33"),sQuery(id+"F4.wireOp",EDGE,"E43"),sQuery(id+"F4.wireOp",EDGE,"E44")])]});
            var Q13;
            Q13=makeQuery(id+"F5.opExtrude","SWEPT_EDGE",EDGE,{"disambiguationData":[OSD([sQuery(id+"F4.wireOp",EDGE,"E41"),sQuery(id+"F4.wireOp",EDGE,"E57.MirrorCS")])]});
            fillet(context, id + "F6", {"entities" : qUnion([Q0, Q1, Q2, Q3, Q4, Q5, Q6, Q7, Q8, Q9, Q10, Q11, Q12, Q13]), "radius" : 5 * mm, "tangentPropagation" : true, "allowEdgeOverflow" : false});
        }
    });
